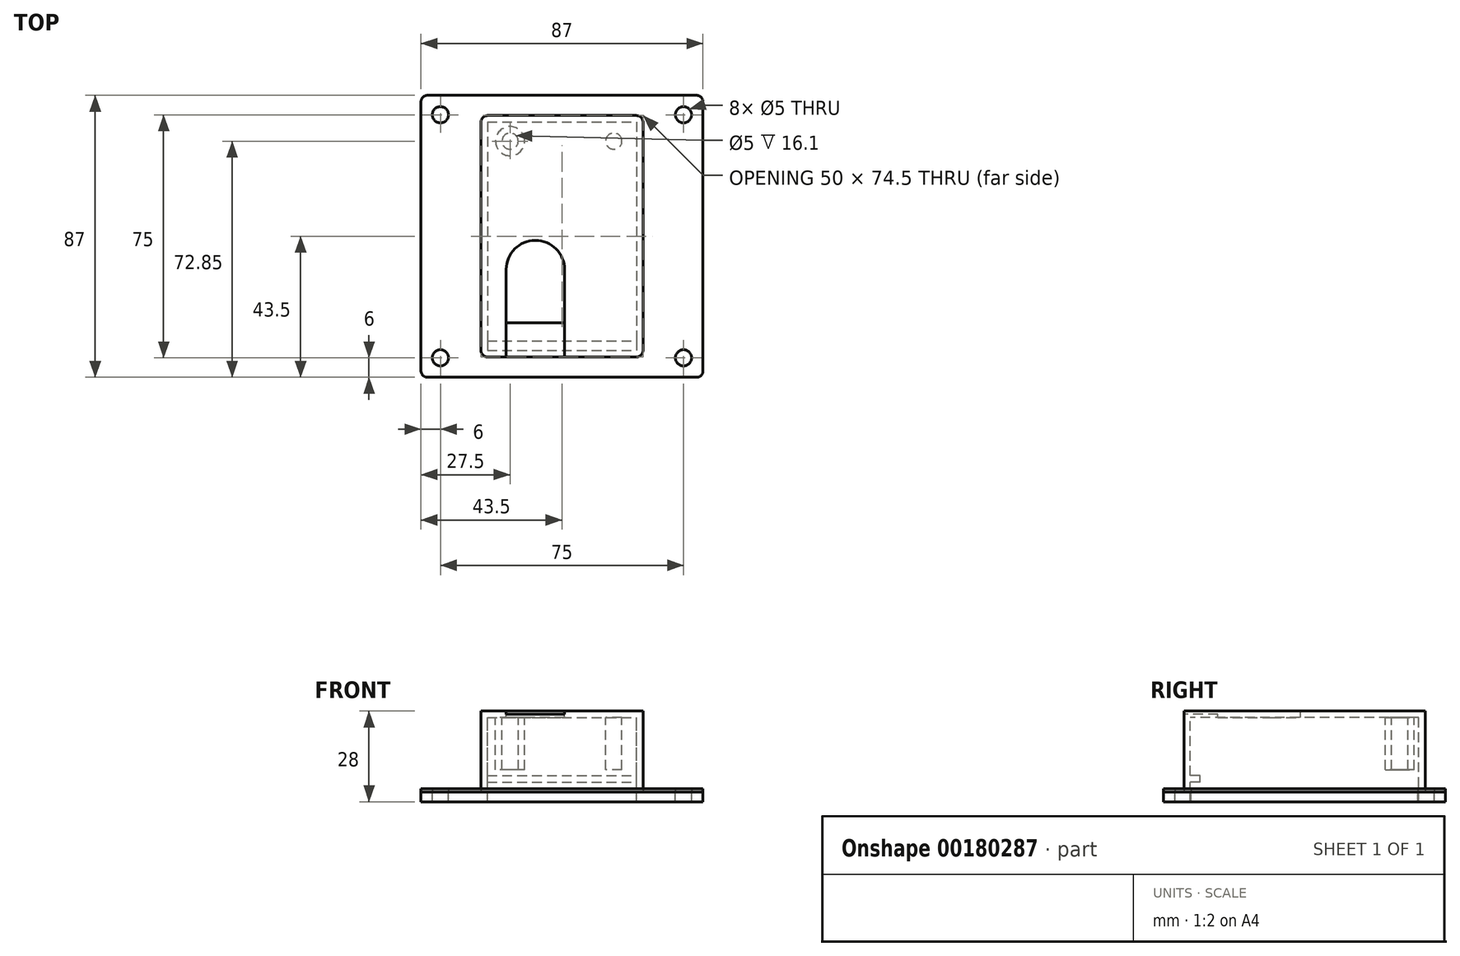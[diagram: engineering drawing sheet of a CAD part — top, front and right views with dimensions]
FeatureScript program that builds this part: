
annotation { "Feature Type Name" : "Feature", "Feature Type Description" : "" }
export const myFeature = defineFeature(function(context is Context, id is Id, definition is map)
    precondition{}
    {
        {
            var Q0;
            Q0=qCreatedBy(makeId("Top.planeOp"),FACE);
            var sketch = newSketch(context, id + "F0", { "sketchPlane" : qUnion([Q0])});
            skLineSegment(sketch, "E0.bottom", {"start": v(-21.5, 33.75) * mm, "end": v(21.5, 33.75) * mm, "construction": true});
            skLineSegment(sketch, "E0.top", {"start": v(-21.5, -33.75) * mm, "end": v(21.5, -33.75) * mm, "construction": true});
            skLineSegment(sketch, "E0.left", {"start": v(-21.5, 33.75) * mm, "end": v(-21.5, -33.75) * mm, "construction": true});
            skLineSegment(sketch, "E0.right", {"start": v(21.5, 33.75) * mm, "end": v(21.5, -33.75) * mm, "construction": true});
            skPoint(sketch, "E0.middle", {"position": v(0, 0) * mm});
            skLineSegment(sketch, "E1.bottom", {"start": v(-17.2, -26.75) * mm, "end": v(0.8, -26.75) * mm});
            skLineSegment(sketch, "E1.top", {"start": v(-17.2, -1.25) * mm, "end": v(0.8, -1.25) * mm});
            skLineSegment(sketch, "E1.left", {"start": v(-17.2, -26.75) * mm, "end": v(-17.2, -1.25) * mm});
            skLineSegment(sketch, "E1.right", {"start": v(0.8, -26.75) * mm, "end": v(0.8, -1.25) * mm});
            skCircle(sketch, "E2", {"center": v(-8.2, -10.25) * mm, "radius": 9 * mm});
            skPoint(sketch, "E2.first.point", {"position": v(-17.2, -10.25) * mm});
            skPoint(sketch, "E2.second.point", {"position": v(0.8, -10.25) * mm});
            skPoint(sketch, "E2.third.point", {"position": v(-8.2, -1.25) * mm});
            skLineSegment(sketch, "E3", {"start": v(0, -33.75) * mm, "end": v(0, 33.75) * mm, "construction": true});
            skCircle(sketch, "E4", {"center": v(-16, 29.35) * mm, "radius": 2.5 * mm});
            skCircle(sketch, "E5.MirrorC", {"center": v(16, 29.35) * mm, "radius": 2.5 * mm});
            skLineSegment(sketch, "E6.0", {"start": v(-23, 35.25) * mm, "end": v(-23, -35.25) * mm});
            skLineSegment(sketch, "E6.1", {"start": v(-23, 35.25) * mm, "end": v(23, 35.25) * mm});
            skLineSegment(sketch, "E6.2", {"start": v(23, 35.25) * mm, "end": v(23, -35.25) * mm});
            skLineSegment(sketch, "E6.3", {"start": v(-23, -35.25) * mm, "end": v(23, -35.25) * mm});
            skLineSegment(sketch, "E7.0", {"start": v(-25, 37.25) * mm, "end": v(-25, -37.25) * mm});
            skLineSegment(sketch, "E7.1", {"start": v(-25, 37.25) * mm, "end": v(25, 37.25) * mm});
            skLineSegment(sketch, "E7.2", {"start": v(25, 37.25) * mm, "end": v(25, -37.25) * mm});
            skLineSegment(sketch, "E7.3", {"start": v(-25, -37.25) * mm, "end": v(25, -37.25) * mm});
            skCircle(sketch, "E8.0", {"center": v(-16, 29.35) * mm, "radius": 4.5 * mm});
            skCircle(sketch, "E9.MirrorC", {"center": v(16, 29.35) * mm, "radius": 4.5 * mm});
            skSolve(sketch);
        }
        {
            var Q0;
            Q0 = qSketchRegion(id + "F0", true);
            var Q1;
            {var subQ6=sQuery(id+"F0.wireOp",EDGE,"E1.bottom");Q1=makeQuery(id+"F0.imprint","IMPRINT",FACE,{"disambiguationData":[TD([[makeQuery(id+"F0.imprint","IMPRINT",EDGE,{"derivedFrom":subQ6}),-1.0]])]});}
            var Q2;
            Q2=makeQuery(id+"F0.imprint","IMPRINT",FACE,{"disambiguationData":[TD([[makeQuery(id+"F0.imprint","IMPRINT",EDGE,{"derivedFrom":sQuery(id+"F0.wireOp",EDGE,"E4")}),1.0]])]});
            var Q3;
            Q3=makeQuery(id+"F0.imprint","IMPRINT",FACE,{"disambiguationData":[TD([[makeQuery(id+"F0.imprint","IMPRINT",EDGE,{"derivedFrom":sQuery(id+"F0.wireOp",EDGE,"E5.MirrorC")}),-1.0]])]});
            var Q4;
            {var subQ0=sQuery(id+"F0.wireOp",EDGE,"E1.left");var subQ1=sQuery(id+"F0.wireOp",EDGE,"E1.top");var subQ2=makeQuery(id+"F0.imprint","INTERSECT",VERTEX,{"derivedFrom":[subQ1,subQ0]});Q4=makeQuery(id+"F0.imprint","IMPRINT",FACE,{"disambiguationData":[TD([[makeQuery(id+"F0.imprint","IMPRINT",EDGE,{"disambiguationData":[TD([[subQ2,-1.0]])],"derivedFrom":subQ1}),-1.0]])]});}
            var Q5;
            {var subQ0=sQuery(id+"F0.wireOp",EDGE,"E1.right");var subQ1=sQuery(id+"F0.wireOp",EDGE,"E1.top");var subQ2=makeQuery(id+"F0.imprint","INTERSECT",VERTEX,{"derivedFrom":[subQ1,subQ0]});Q5=makeQuery(id+"F0.imprint","IMPRINT",FACE,{"disambiguationData":[TD([[makeQuery(id+"F0.imprint","IMPRINT",EDGE,{"disambiguationData":[TD([[subQ2,1.0]])],"derivedFrom":subQ1}),-1.0]])]});}
            var Q6;
            Q6=makeQuery(id+"F0.imprint","IMPRINT",FACE,{"disambiguationData":[TD([[makeQuery(id+"F0.imprint","IMPRINT",EDGE,{"derivedFrom":sQuery(id+"F0.wireOp",EDGE,"E4")}),-1.0]])]});
            var Q7;
            Q7=makeQuery(id+"F0.imprint","IMPRINT",FACE,{"disambiguationData":[TD([[makeQuery(id+"F0.imprint","IMPRINT",EDGE,{"derivedFrom":sQuery(id+"F0.wireOp",EDGE,"E5.MirrorC")}),1.0]])]});
            extrude(context, id + "F1", {"entities" : qUnion([Q0, Q1, Q2, Q3, Q4, Q5, Q6, Q7]), "oppositeDirection" : true, "depth" : 2 * mm});
        }
        {
            var Q0;
            Q0=makeQuery(id+"F0.imprint","IMPRINT",FACE,{"disambiguationData":[TD([[makeQuery(id+"F0.imprint","IMPRINT",EDGE,{"derivedFrom":sQuery(id+"F0.wireOp",EDGE,"E6.0")}),-1.0]])]});
            extrude(context, id + "F2", {"entities" : qUnion([Q0]), "operationType" : NewBodyOperationType.ADD, "oppositeDirection" : true, "depth" : 25 * mm});
        }
        {
            var Q0;
            Q0=makeQuery(id+"F0.imprint","IMPRINT",FACE,{"disambiguationData":[TD([[makeQuery(id+"F0.imprint","IMPRINT",EDGE,{"derivedFrom":sQuery(id+"F0.wireOp",EDGE,"E4")}),-1.0]])]});
            var Q1;
            Q1=makeQuery(id+"F0.imprint","IMPRINT",FACE,{"disambiguationData":[TD([[makeQuery(id+"F0.imprint","IMPRINT",EDGE,{"derivedFrom":sQuery(id+"F0.wireOp",EDGE,"E5.MirrorC")}),1.0]])]});
            extrude(context, id + "F3", {"entities" : qUnion([Q0, Q1]), "operationType" : NewBodyOperationType.ADD, "oppositeDirection" : true, "depth" : 18.1 * mm});
        }
        {
            var Q0;
            Q0=makeQuery(id+"F2.opExtrude","SWEPT_FACE",FACE,{"disambiguationData":[OSD([sQuery(id+"F0.wireOp",EDGE,"E6.3")])]});
            var sketch = newSketch(context, id + "F4", { "sketchPlane" : qUnion([Q0])});
            skLineSegment(sketch, "E10.0", {"start": v(23, -19.9) * mm, "end": v(-23, -19.9) * mm});
            skLineSegment(sketch, "E11.0", {"start": v(23, -21.9) * mm, "end": v(-23, -21.9) * mm});
            skSolve(sketch);
        }
        {
            var Q0;
            {var subQ0=sQuery(id+"F4.wireOp",EDGE,"E10.0");Q0=makeQuery(id+"F4.imprint","IMPRINT",FACE,{"disambiguationData":[TD([[makeQuery(id+"F4.imprint","IMPRINT",EDGE,{"derivedFrom":subQ0}),1.0]])]});}
            extrude(context, id + "F5", {"entities" : qUnion([Q0]), "operationType" : NewBodyOperationType.ADD, "depth" : 3 * mm});
        }
        {
            var Q0;
            Q0=makeQuery(id+"F2.opExtrude","CAP_FACE",FACE,{"disambiguationData":[OSD([sQuery(id+"F0.wireOp",EDGE,"E6.0"),sQuery(id+"F0.wireOp",EDGE,"E6.1"),sQuery(id+"F0.wireOp",EDGE,"E6.2"),sQuery(id+"F0.wireOp",EDGE,"E6.3"),sQuery(id+"F0.wireOp",EDGE,"E7.0"),sQuery(id+"F0.wireOp",EDGE,"E7.1"),sQuery(id+"F0.wireOp",EDGE,"E7.2"),sQuery(id+"F0.wireOp",EDGE,"E7.3")])],"isStart":false});
            var sketch = newSketch(context, id + "F6", { "sketchPlane" : qUnion([Q0])});
            skLineSegment(sketch, "E12.bottom", {"start": v(37.5, -37.5) * mm, "end": v(-37.5, -37.5) * mm, "construction": true});
            skLineSegment(sketch, "E12.top", {"start": v(37.5, 37.5) * mm, "end": v(-37.5, 37.5) * mm, "construction": true});
            skLineSegment(sketch, "E12.left", {"start": v(37.5, -37.5) * mm, "end": v(37.5, 37.5) * mm, "construction": true});
            skLineSegment(sketch, "E12.right", {"start": v(-37.5, -37.5) * mm, "end": v(-37.5, 37.5) * mm, "construction": true});
            skPoint(sketch, "E12.middle", {"position": v(0, 0) * mm});
            skLineSegment(sketch, "E13.0", {"start": v(43.5, -43.5) * mm, "end": v(-43.5, -43.5) * mm});
            skLineSegment(sketch, "E13.1", {"start": v(43.5, -43.5) * mm, "end": v(43.5, 43.5) * mm});
            skLineSegment(sketch, "E13.2", {"start": v(43.5, 43.5) * mm, "end": v(-43.5, 43.5) * mm});
            skLineSegment(sketch, "E13.3", {"start": v(-43.5, -43.5) * mm, "end": v(-43.5, 43.5) * mm});
            skCircle(sketch, "E14", {"center": v(37.5, -37.5) * mm, "radius": 2.5 * mm});
            skLineSegment(sketch, "E15", {"start": v(0, -43.5) * mm, "end": v(0, 43.5) * mm, "construction": true});
            skLineSegment(sketch, "E16", {"start": v(43.5, 0) * mm, "end": v(-43.5, 0) * mm, "construction": true});
            skCircle(sketch, "E17.MirrorC", {"center": v(-37.5, -37.5) * mm, "radius": 2.5 * mm});
            skCircle(sketch, "E18.MirrorC", {"center": v(37.5, 37.5) * mm, "radius": 2.5 * mm});
            skCircle(sketch, "E19.MirrorC", {"center": v(-37.5, 37.5) * mm, "radius": 2.5 * mm});
            skSolve(sketch);
        }
        {
            var Q0;
            Q0=makeQuery(id+"F6.imprint","IMPRINT",FACE,{"disambiguationData":[TD([[makeQuery(id+"F6.imprint","IMPRINT",EDGE,{"derivedFrom":sQuery(id+"F6.wireOp",EDGE,"E13.0")}),-1.0]])]});
            var Q1;
            Q1=makeQuery(id+"F6.imprint","IMPRINT",FACE,{"disambiguationData":[TD([[makeQuery(id+"F6.imprint","IMPRINT",EDGE,{"derivedFrom":makeQuery(id+"F2.opExtrude","CAP_EDGE",EDGE,{"disambiguationData":[OSD([sQuery(id+"F0.wireOp",EDGE,"E6.0")])],"isStart":false})}),1.0]])]});
            extrude(context, id + "F7", {"entities" : qUnion([Q0, Q1]), "operationType" : NewBodyOperationType.ADD, "depth" : 3 * mm});
        }
        {
            var Q0;
            {var subQ0=sQuery(id+"F0.wireOp",EDGE,"E7.3");var subQ1=sQuery(id+"F0.wireOp",EDGE,"E7.2");Q0=makeQuery(id+"F2.boolean.opBoolean","MERGE",EDGE,{"derivedFrom":[makeQuery(id+"F1.opExtrude","SWEPT_EDGE",EDGE,{"disambiguationData":[OSD([subQ1,subQ0])]}),makeQuery(id+"F2.opExtrude","SWEPT_EDGE",EDGE,{"disambiguationData":[OSD([subQ1,subQ0])]})]});}
            var Q1;
            Q1=makeQuery(id+"F7.opExtrude","SWEPT_EDGE",EDGE,{"disambiguationData":[OSD([sQuery(id+"F6.wireOp",EDGE,"E13.1"),sQuery(id+"F6.wireOp",EDGE,"E13.2")])]});
            var Q2;
            Q2=makeQuery(id+"F7.opExtrude","SWEPT_EDGE",EDGE,{"disambiguationData":[OSD([sQuery(id+"F6.wireOp",EDGE,"E13.2"),sQuery(id+"F6.wireOp",EDGE,"E13.3")])]});
            var Q3;
            Q3=makeQuery(id+"F7.opExtrude","SWEPT_EDGE",EDGE,{"disambiguationData":[OSD([sQuery(id+"F6.wireOp",EDGE,"E13.0"),sQuery(id+"F6.wireOp",EDGE,"E13.1")])]});
            var Q4;
            Q4=makeQuery(id+"F7.opExtrude","SWEPT_EDGE",EDGE,{"disambiguationData":[OSD([sQuery(id+"F6.wireOp",EDGE,"E13.0"),sQuery(id+"F6.wireOp",EDGE,"E13.3")])]});
            var Q5;
            {var subQ0=sQuery(id+"F0.wireOp",EDGE,"E7.1");var subQ1=sQuery(id+"F0.wireOp",EDGE,"E7.0");Q5=makeQuery(id+"F2.boolean.opBoolean","MERGE",EDGE,{"derivedFrom":[makeQuery(id+"F1.opExtrude","SWEPT_EDGE",EDGE,{"disambiguationData":[OSD([subQ1,subQ0])]}),makeQuery(id+"F2.opExtrude","SWEPT_EDGE",EDGE,{"disambiguationData":[OSD([subQ1,subQ0])]})]});}
            var Q6;
            {var subQ0=sQuery(id+"F0.wireOp",EDGE,"E7.2");var subQ1=sQuery(id+"F0.wireOp",EDGE,"E7.1");Q6=makeQuery(id+"F2.boolean.opBoolean","MERGE",EDGE,{"derivedFrom":[makeQuery(id+"F1.opExtrude","SWEPT_EDGE",EDGE,{"disambiguationData":[OSD([subQ1,subQ0])]}),makeQuery(id+"F2.opExtrude","SWEPT_EDGE",EDGE,{"disambiguationData":[OSD([subQ1,subQ0])]})]});}
            var Q7;
            {var subQ0=sQuery(id+"F0.wireOp",EDGE,"E7.3");var subQ1=sQuery(id+"F0.wireOp",EDGE,"E7.0");Q7=makeQuery(id+"F2.boolean.opBoolean","MERGE",EDGE,{"derivedFrom":[makeQuery(id+"F1.opExtrude","SWEPT_EDGE",EDGE,{"disambiguationData":[OSD([subQ1,subQ0])]}),makeQuery(id+"F2.opExtrude","SWEPT_EDGE",EDGE,{"disambiguationData":[OSD([subQ1,subQ0])]})]});}
            fillet(context, id + "F8", {"entities" : qUnion([Q0, Q1, Q2, Q3, Q4, Q5, Q6, Q7]), "radius" : 2 * mm, "tangentPropagation" : true, "allowEdgeOverflow" : false});
        }
        {
            var Q0;
            Q0=makeQuery(id+"F7.opExtrude","CAP_FACE",FACE,{"disambiguationData":[OSD([sQuery(id+"F0.wireOp",EDGE,"E6.0"),sQuery(id+"F0.wireOp",EDGE,"E6.1"),sQuery(id+"F0.wireOp",EDGE,"E6.2"),sQuery(id+"F0.wireOp",EDGE,"E6.3"),sQuery(id+"F6.wireOp",EDGE,"E13.0"),sQuery(id+"F6.wireOp",EDGE,"E13.1"),sQuery(id+"F6.wireOp",EDGE,"E13.2"),sQuery(id+"F6.wireOp",EDGE,"E13.3"),sQuery(id+"F6.wireOp",EDGE,"E14"),sQuery(id+"F6.wireOp",EDGE,"E17.MirrorC"),sQuery(id+"F6.wireOp",EDGE,"E18.MirrorC"),sQuery(id+"F6.wireOp",EDGE,"E19.MirrorC")])],"isStart":true});
            extrude(context, id + "F9", {"entities" : qUnion([Q0]), "depth" : 1 * mm});
        }
        {
            var Q0;
            {var subQ0=sQuery(id+"F0.wireOp",EDGE,"E7.3");Q0=makeQuery(id+"F2.boolean.opBoolean","MERGE",FACE,{"derivedFrom":[makeQuery(id+"F1.opExtrude","SWEPT_FACE",FACE,{"disambiguationData":[OSD([subQ0])]}),makeQuery(id+"F2.opExtrude","SWEPT_FACE",FACE,{"disambiguationData":[OSD([subQ0])]})]});}
            var sketch = newSketch(context, id + "F10", { "sketchPlane" : qUnion([Q0])});
            skLineSegment(sketch, "E20.bottom", {"start": v(-17.2, 0) * mm, "end": v(0.8, 0) * mm});
            skLineSegment(sketch, "E20.top", {"start": v(-17.2, -1) * mm, "end": v(0.8, -1) * mm});
            skLineSegment(sketch, "E20.left", {"start": v(-17.2, 0) * mm, "end": v(-17.2, -1) * mm});
            skLineSegment(sketch, "E20.right", {"start": v(0.8, 0) * mm, "end": v(0.8, -1) * mm});
            skSolve(sketch);
        }
        {
            var Q0;
            Q0 = qSketchRegion(id + "F10", true);
            extrude(context, id + "F11", {"entities" : qUnion([Q0]), "operationType" : NewBodyOperationType.REMOVE, "oppositeDirection" : true, "depth" : 25 * mm});
        }
    });
